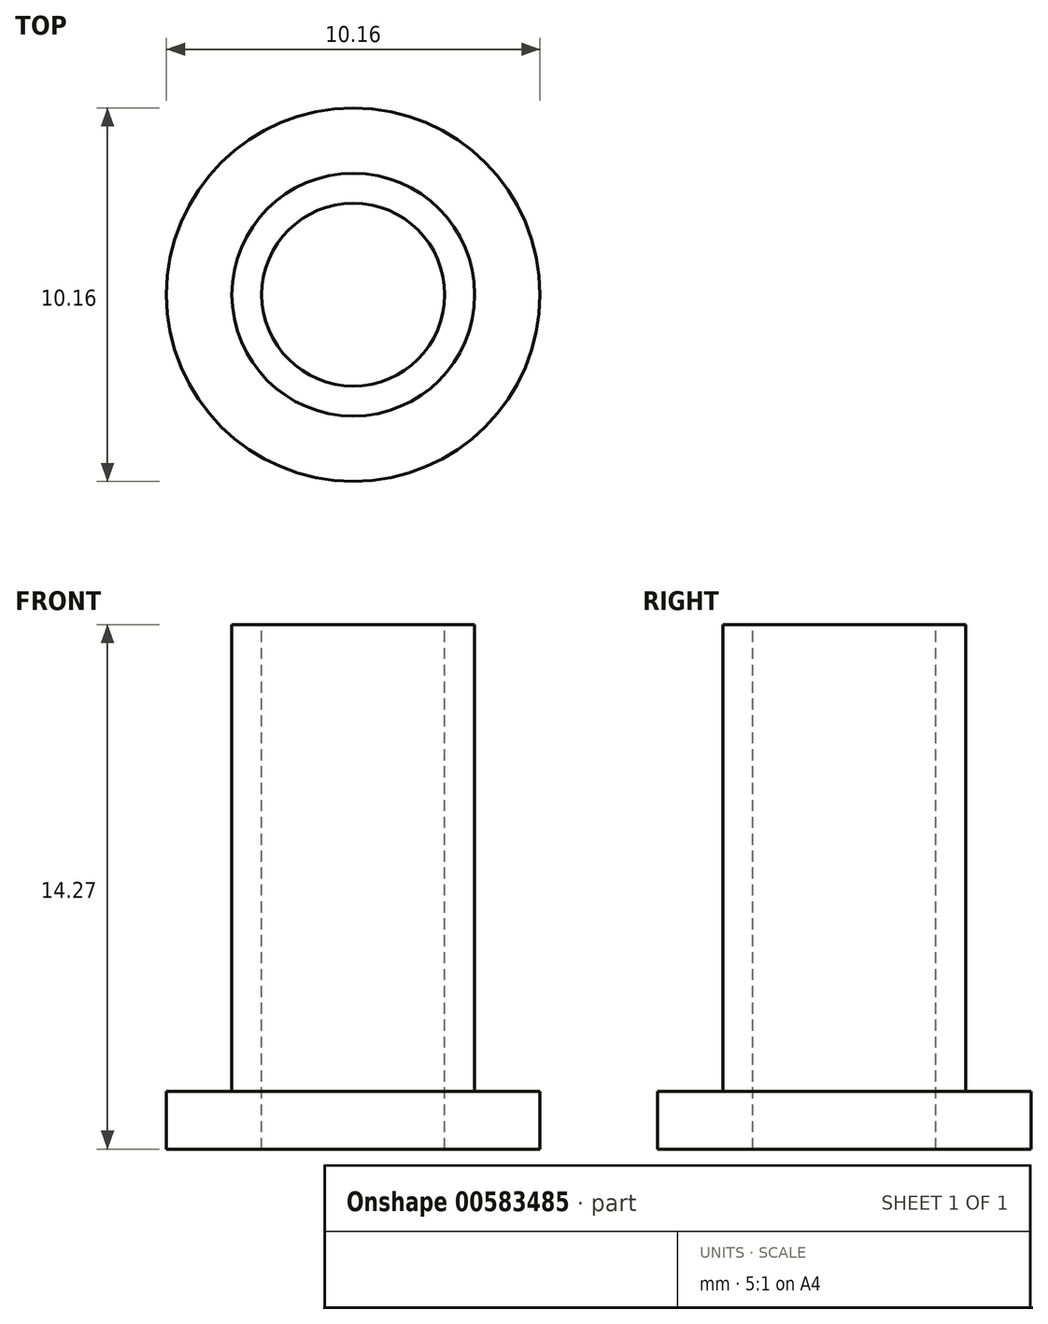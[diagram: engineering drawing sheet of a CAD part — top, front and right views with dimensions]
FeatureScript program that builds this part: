
annotation { "Feature Type Name" : "Feature", "Feature Type Description" : "" }
export const myFeature = defineFeature(function(context is Context, id is Id, definition is map)
    precondition{}
    {
        {
            var Q0;
            Q0=qCreatedBy(makeId("Top.planeOp"),FACE);
            var sketch = newSketch(context, id + "F0", { "sketchPlane" : qUnion([Q0])});
            skCircle(sketch, "E0", {"center": v(0, 0) * mm, "radius": 5.08 * mm});
            skSolve(sketch);
        }
        {
            var Q0;
            Q0=qSketchRegion(id+"F0",true);
            extrude(context, id + "F1", {"entities" : qUnion([Q0]), "depth" : 14.27 * mm});
        }
        {
            var Q0;
            Q0=makeQuery(id+"F1.opExtrude","CAP_FACE",FACE,{"disambiguationData":[OSD([sQuery(id+"F0.wireOp",EDGE,"E0")])],"isStart":false});
            var sketch = newSketch(context, id + "F2", { "sketchPlane" : qUnion([Q0])});
            skCircle(sketch, "E1", {"center": v(0, 0) * mm, "radius": 5.08 * mm});
            skCircle(sketch, "E2", {"center": v(0, 0) * mm, "radius": 3.3 * mm});
            skSolve(sketch);
        }
        {
            var Q0;
            Q0=qSketchRegion(id+"F2",true);
            extrude(context, id + "F3", {"entities" : qUnion([Q0]), "operationType" : NewBodyOperationType.REMOVE, "oppositeDirection" : true, "depth" : 12.7 * mm});
        }
        {
            var Q0;
            Q0=makeQuery(id+"F1.opExtrude","CAP_FACE",FACE,{"disambiguationData":[OSD([sQuery(id+"F0.wireOp",EDGE,"E0")])],"isStart":false});
            var sketch = newSketch(context, id + "F4", { "sketchPlane" : qUnion([Q0])});
            skCircle(sketch, "E3", {"center": v(0, 0) * mm, "radius": 2.49 * mm});
            skSolve(sketch);
        }
        {
            var Q0;
            Q0=qSketchRegion(id+"F4",true);
            extrude(context, id + "F5", {"entities" : qUnion([Q0]), "operationType" : NewBodyOperationType.REMOVE, "oppositeDirection" : true, "depth" : 14.27 * mm});
        }
    });
